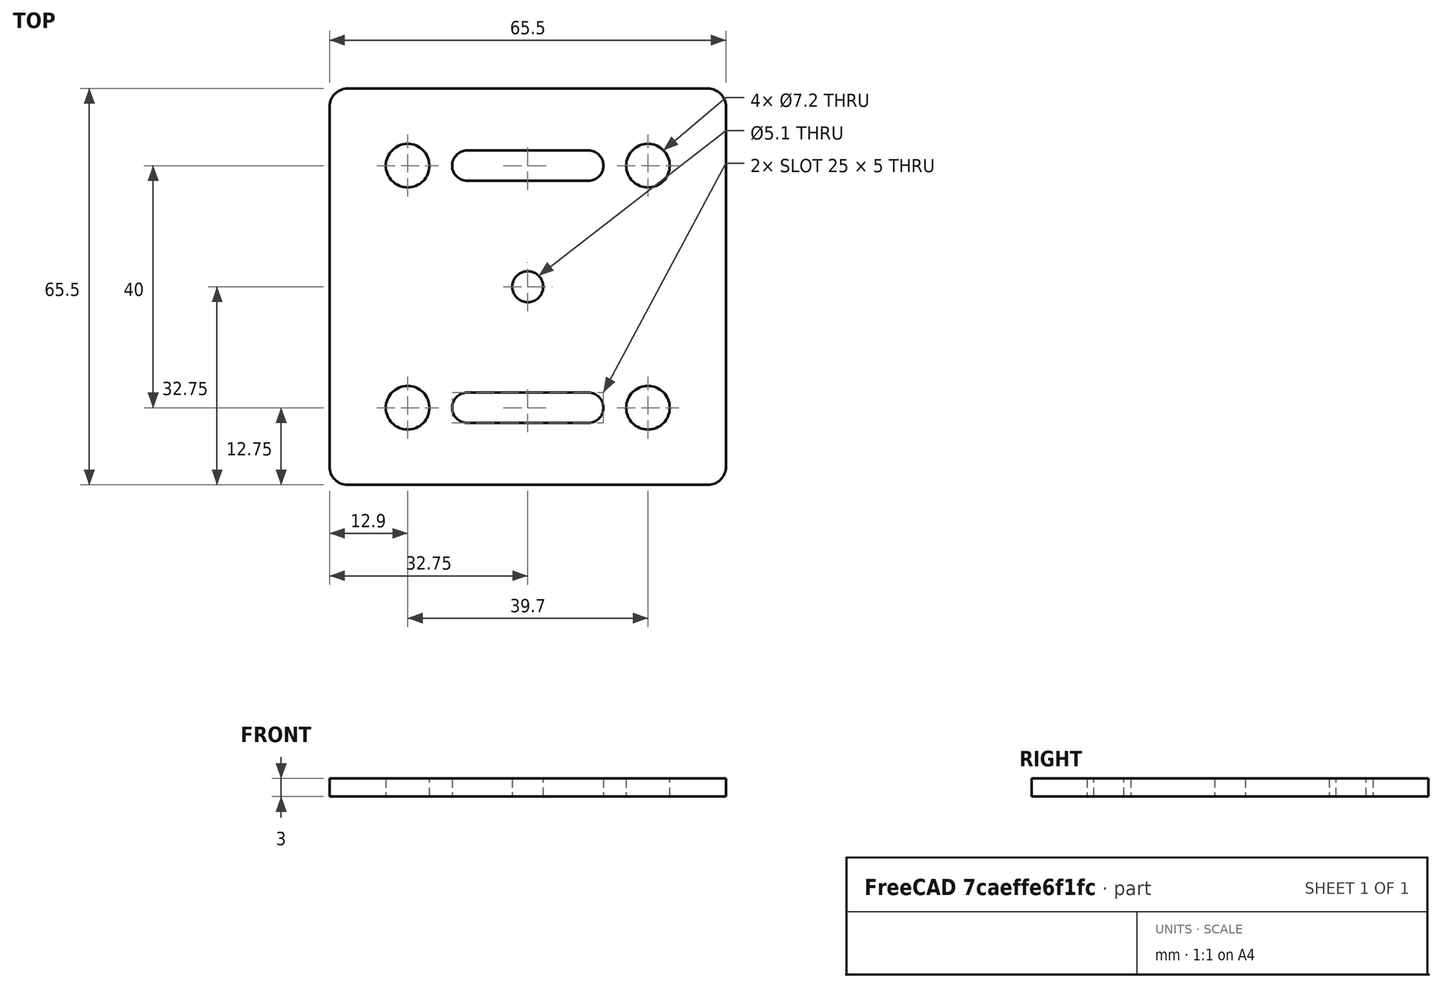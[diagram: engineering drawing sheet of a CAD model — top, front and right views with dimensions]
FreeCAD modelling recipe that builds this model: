
FCSTD DOCUMENT  (FreeCAD 0.20R29410 (Git))
Label: GantryBracket
License: All rights reserved
LicenseURL: http://en.wikipedia.org/wiki/All_rights_reserved
objects: PartDesign::CoordinateSystem×5, App::DocumentObjectGroup×3, App::FeaturePython×1, Sketcher::SketchObject×1, PartDesign::Pad×1, PartDesign::Body×1, App::Part×1
note: 9 computed .brp shape members not serialized (recipe doc carries the construction recipe); baked Part::Feature solids carry a one-line shape summary decoded from their .brp

FEATURE [App::DocumentObjectGroup] Parts
FEATURE [PartDesign::CoordinateSystem] LCS_Origin
  AttacherType = Attacher::AttachEngine3D
  MapMode = 2
  Support = -> [X_Axis]
FEATURE [App::FeaturePython] Variables  # WARN: FeaturePython — macro-defined, semantics opaque (R4)
  Type = App::PropertyContainer
FEATURE [App::DocumentObjectGroup] Constraints
FEATURE [App::DocumentObjectGroup] Configurations
FEATURE [Sketcher::SketchObject] Sketch
  FullyConstrained = true
  MapMode = 5
  Support = -> [XY_Plane001]
  sketch-geometry (26):
    g0: ArcOfCircle CenterX=-29.75 CenterY=29.75 CenterZ=0 NormalX=0 NormalY=0 NormalZ=1 AngleXU=0 Radius=3 StartAngle=1.5708 EndAngle=3.14159
    g1: LineSegment StartX=-29.75 StartY=32.75 StartZ=0 EndX=29.75 EndY=32.75 EndZ=0
    g2: ArcOfCircle CenterX=29.75 CenterY=29.75 CenterZ=0 NormalX=0 NormalY=0 NormalZ=1 AngleXU=0 Radius=3 StartAngle=5e-16 EndAngle=1.5708
    g3: LineSegment StartX=32.75 StartY=29.75 StartZ=0 EndX=32.75 EndY=-29.75 EndZ=0
    g4: ArcOfCircle CenterX=29.75 CenterY=-29.75 CenterZ=0 NormalX=0 NormalY=0 NormalZ=1 AngleXU=0 Radius=3 StartAngle=4.71239 EndAngle=6.28319
    g5: LineSegment StartX=29.75 StartY=-32.75 StartZ=0 EndX=-29.75 EndY=-32.75 EndZ=0
    g6: ArcOfCircle CenterX=-29.75 CenterY=-29.75 CenterZ=0 NormalX=0 NormalY=0 NormalZ=1 AngleXU=0 Radius=3 StartAngle=3.14159 EndAngle=4.71239
    g7: LineSegment StartX=-32.75 StartY=-29.75 StartZ=0 EndX=-32.75 EndY=29.75 EndZ=0
    g8: GeomPoint X=-32.75 Y=32.75 Z=0
    g9: GeomPoint X=32.75 Y=-32.75 Z=0
    g10: Circle CenterX=0 CenterY=0 CenterZ=0 NormalX=0 NormalY=0 NormalZ=1 AngleXU=0 Radius=2.55
    g11: Circle CenterX=-19.85 CenterY=-20 CenterZ=0 NormalX=0 NormalY=0 NormalZ=1 AngleXU=0 Radius=3.6
    g12: Circle CenterX=19.85 CenterY=-20 CenterZ=0 NormalX=0 NormalY=0 NormalZ=1 AngleXU=0 Radius=3.6
    g13: Circle CenterX=19.85 CenterY=20 CenterZ=0 NormalX=0 NormalY=0 NormalZ=1 AngleXU=0 Radius=3.6
    g14: Circle CenterX=-19.85 CenterY=20 CenterZ=0 NormalX=0 NormalY=0 NormalZ=1 AngleXU=0 Radius=3.6
    g15: LineSegment StartX=-19.85 StartY=20 StartZ=0 EndX=19.85 EndY=20 EndZ=0
    g16: LineSegment StartX=19.85 StartY=20 StartZ=0 EndX=19.85 EndY=-20 EndZ=0
    g17: ArcOfCircle CenterX=-10 CenterY=-20 CenterZ=0 NormalX=0 NormalY=0 NormalZ=1 AngleXU=0 Radius=2.5 StartAngle=1.5708 EndAngle=4.71239
    g18: ArcOfCircle CenterX=10 CenterY=-20 CenterZ=0 NormalX=0 NormalY=0 NormalZ=1 AngleXU=0 Radius=2.5 StartAngle=4.71239 EndAngle=7.85398
    g19: LineSegment StartX=-10 StartY=-22.5 StartZ=0 EndX=10 EndY=-22.5 EndZ=0
    g20: LineSegment StartX=10 StartY=-17.5 StartZ=0 EndX=-10 EndY=-17.5 EndZ=0
    g21: ArcOfCircle CenterX=-10 CenterY=20 CenterZ=0 NormalX=0 NormalY=0 NormalZ=1 AngleXU=0 Radius=2.5 StartAngle=1.5708 EndAngle=4.71239
    g22: ArcOfCircle CenterX=10 CenterY=20 CenterZ=0 NormalX=0 NormalY=0 NormalZ=1 AngleXU=0 Radius=2.5 StartAngle=4.71239 EndAngle=7.85398
    g23: LineSegment StartX=-10 StartY=17.5 StartZ=0 EndX=10 EndY=17.5 EndZ=0
    g24: LineSegment StartX=10 StartY=22.5 StartZ=0 EndX=-10 EndY=22.5 EndZ=0
    g25: LineSegment StartX=10 StartY=17.5 StartZ=0 EndX=10 EndY=-17.5 EndZ=0
  constraints (60):
    c: Tangent(g0,g1) = 1.5708
    c: Tangent(g1,g2) = 1.5708
    c: Tangent(g2,g3) = 1.5708
    c: Tangent(g3,g4) = 1.5708
    c: Tangent(g4,g5) = 1.5708
    c: Tangent(g5,g6) = 1.5708
    c: Tangent(g6,g7) = 1.5708
    c: Tangent(g7,g0) = 1.5708
    c: Horizontal(g1)
    c: Horizontal(g5)
    c: Vertical(g3)
    c: Vertical(g7)
    c: Equal(g0,g2)
    c: Equal(g2,g4)
    c: Equal(g4,g6)
    c: PointOnObject(g8,g1)
    c: PointOnObject(g8,g7)
    c: PointOnObject(g9,g3)
    c: PointOnObject(g9,g5)
    c: Symmetric(g2,g6,g-1)
    c: DistanceY(g4,g1) = 65.5
    c: Equal(g1,g3)
    c: Radius(g2) = 3
    c: Coincident(g10,g-1)
    c: Equal(g11,g12)
    c: Equal(g12,g13)
    c: Equal(g13,g14)
    c: Coincident(g15,g14)
    c: Coincident(g15,g13)
    c: Coincident(g16,g13)
    c: Coincident(g16,g12)
    c: Vertical(g16)
    c: Horizontal(g15)
    c: Symmetric(g13,g11,g10)
    c: Symmetric(g12,g14,g10)
    c: DistanceY(g14,g0) = 12.75
    c: DistanceX(g0,g14) = 12.9
    c: Diameter(g13) = 7.2
    c: Diameter(g10) = 5.1
    c: Tangent(g17,g19) = -1.5708
    c: Tangent(g19,g18) = -1.5708
    c: Tangent(g18,g20) = -1.5708
    c: Tangent(g20,g17) = -1.5708
    c: Equal(g17,g18)
    c: Horizontal(g19)
    c: Tangent(g21,g23) = -1.5708
    c: Tangent(g23,g22) = -1.5708
    c: Tangent(g22,g24) = -1.5708
    c: Tangent(g24,g21) = -1.5708
    c: Equal(g21,g22)
    c: Equal(g22,g18)
    c: Equal(g20,g23)
    c: Diameter(g22) = 5
    c: Symmetric(g18,g21,g10)
    c: Horizontal(g23)
    c: PointOnObject(g22,g15)
    c: Coincident(g25,g22)
    c: Coincident(g25,g18)
    c: Vertical(g25)
    c: DistanceX(g24,g24) = 20
FEATURE [PartDesign::Pad] Pad
  Direction = (0,0,1)
  Length = 3
  Length2 = 10
  Profile = -> Sketch
  ReferenceAxis = -> Sketch [N_Axis]
  Type = 0
FEATURE [PartDesign::Body] Body
  Group = -> [Sketch,Pad]
  Origin = -> Origin001
  Tip = -> Pad
FEATURE [PartDesign::CoordinateSystem] LCS_wheel1
  AttacherType = Attacher::AttachEngine3D
  MapMode = 11
  Placement = pos=(-19.85,20,3) rot=(0,0,1;1.5708rad)
  Support = -> [Pad]
FEATURE [PartDesign::CoordinateSystem] LCS_wheel2
  AttacherType = Attacher::AttachEngine3D
  MapMode = 11
  Placement = pos=(19.85,20,3) rot=(0,0,1;1.5708rad)
  Support = -> [Pad]
FEATURE [PartDesign::CoordinateSystem] LCS_wheel3
  AttacherType = Attacher::AttachEngine3D
  MapMode = 11
  Placement = pos=(-19.85,-20,3) rot=(0,0,1;1.5708rad)
  Support = -> [Pad]
FEATURE [PartDesign::CoordinateSystem] LCS_wheel4
  AttacherType = Attacher::AttachEngine3D
  MapMode = 11
  Placement = pos=(19.85,-20,3) rot=(0,0,1;1.5708rad)
  Support = -> [Pad]
FEATURE [App::Part] Assembly
  AssemblyType = Part::Link
  Group = -> [LCS_Origin,Variables,Constraints,Configurations,Body,LCS_wheel1,LCS_wheel2,LCS_wheel3,LCS_wheel4]
  Origin = -> Origin
  Type = Assembly
